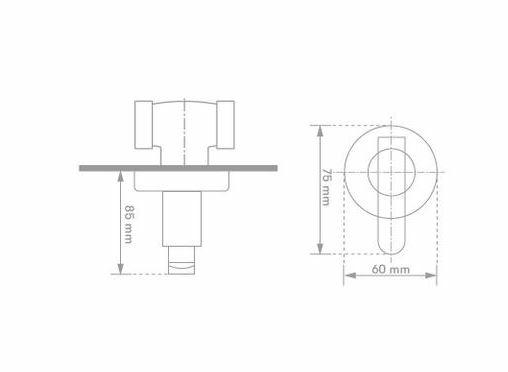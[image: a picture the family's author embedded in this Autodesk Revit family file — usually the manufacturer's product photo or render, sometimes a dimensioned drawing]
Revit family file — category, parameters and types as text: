
# Revit family: 01-1735-11SR-MEZCLADOR HELIX PALA
name_source: partatom
category: Aparatos sanitarios
revit_build: Autodesk Revit 2018 (Build: 20170223_1515(x64)
units: mm (PartAtom-declared; Revit-internal decimal feet)

## family parameters
Anfitrión = Cara
Compartido = No
Corte con vacíos al cargar = No
Cota de conector redondo = Diámetro de uso
Número OmniClass = 23.31.11.00
Punto de cálculo de habitación = No
Tipo de pieza = Normal

## types (1)
- 01-1735-11SR
    Alto = 60 mm  [stored 0.19685 ft]
    Ancho = 60 mm  [stored 0.19685 ft]
    Conexión AC = Sí
    Conexión AF = Sí
    Conexión de residuos = No
    Conexión de ventilación = No
    Descripción = Mezclador ducha
    Distancia entre griferias = 203 mm
    Elevación por defecto = 0 mm  [stored 0 ft]
    Fabricante = Gricol
    Imagen de tipo = <Ninguno>
    Link Ficha Tecnica = https://infotecnica.gricol.com
    Modelo = 01-1735-11SR
    Plastico ABS Cromado = Plastico ABS Cromado
    Product Name = MEZCLADOR 8 SST HELIX PALA
    Profundidad = 85 mm  [stored 0.278871 ft]
    URL = https://www.gricol.com

note: [stored X ft] marks values corroborated as IEEE doubles in the binary element streams (Revit-internal decimal feet)

## geometry (parser evidence)
native form markers: Blend x2, Sweep x10
no freeform markers — native parametric forms only
